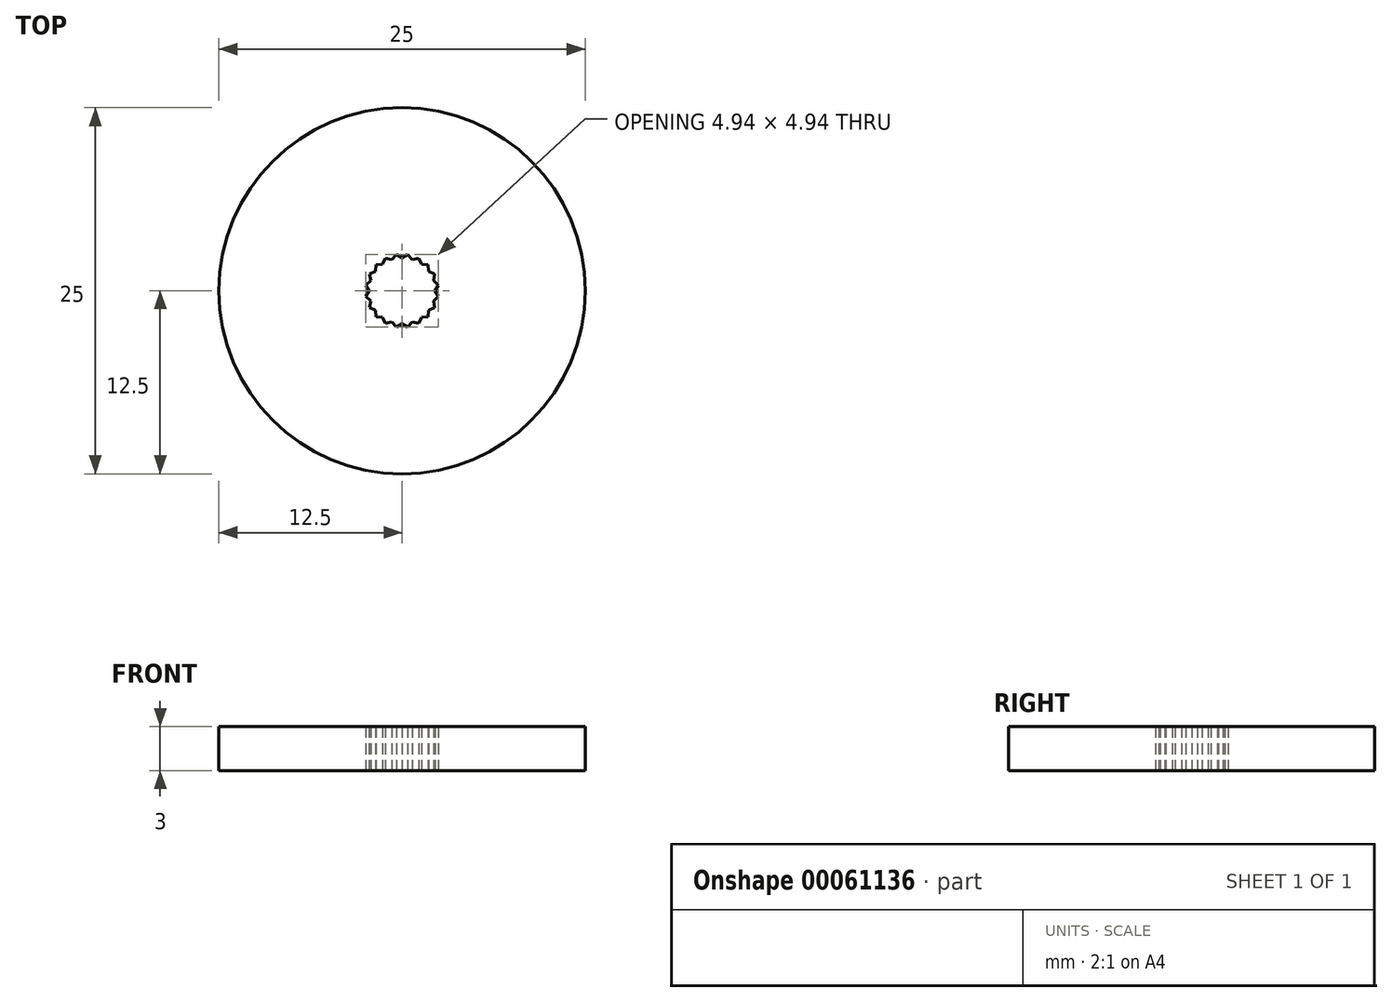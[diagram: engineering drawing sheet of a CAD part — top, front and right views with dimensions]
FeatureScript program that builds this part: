
annotation { "Feature Type Name" : "Feature", "Feature Type Description" : "" }
export const myFeature = defineFeature(function(context is Context, id is Id, definition is map)
    precondition{}
    {
        {
            var Q0;
            Q0=qCreatedBy(makeId("Top.planeOp"),FACE);
            var sketch = newSketch(context, id + "F0", { "sketchPlane" : qUnion([Q0])});
            skCircle(sketch, "E0", {"center": v(0, 0) * mm, "radius": 12.5 * mm});
            skCircle(sketch, "E1", {"center": v(0, 0) * mm, "radius": 2.25 * mm, "construction": true});
            skLineSegment(sketch, "E2", {"start": v(0, 0) * mm, "end": v(2.25, 0) * mm, "construction": true});
            skLineSegment(sketch, "E3", {"start": v(0, 0) * mm, "end": v(2.14, -0.7) * mm, "construction": true});
            skCircle(sketch, "E4", {"center": v(0, 0) * mm, "radius": 2.5 * mm, "construction": true});
            skLineSegment(sketch, "E5", {"start": v(0, 0) * mm, "end": v(2.47, -0.4) * mm, "construction": true});
            skLineSegment(sketch, "E6", {"start": v(2.25, 0) * mm, "end": v(2.47, -0.4) * mm});
            skLineSegment(sketch, "E7", {"start": v(2.47, -0.4) * mm, "end": v(2.14, -0.7) * mm});
            skLineSegment(sketch, "E8.1.0", {"start": v(2.14, 0.7) * mm, "end": v(2.47, 0.4) * mm});
            skLineSegment(sketch, "E8.1.1", {"start": v(2.47, 0.4) * mm, "end": v(2.25, 0) * mm});
            skLineSegment(sketch, "E8.2.0", {"start": v(1.82, 1.32) * mm, "end": v(2.23, 1.13) * mm});
            skLineSegment(sketch, "E8.2.1", {"start": v(2.23, 1.13) * mm, "end": v(2.14, 0.7) * mm});
            skLineSegment(sketch, "E8.3.0", {"start": v(1.32, 1.82) * mm, "end": v(1.77, 1.77) * mm});
            skLineSegment(sketch, "E8.3.1", {"start": v(1.77, 1.77) * mm, "end": v(1.82, 1.32) * mm});
            skLineSegment(sketch, "E8.4.0", {"start": v(0.7, 2.14) * mm, "end": v(1.13, 2.23) * mm});
            skLineSegment(sketch, "E8.4.1", {"start": v(1.13, 2.23) * mm, "end": v(1.32, 1.82) * mm});
            skLineSegment(sketch, "E8.5.0", {"start": v(0, 2.25) * mm, "end": v(0.4, 2.47) * mm});
            skLineSegment(sketch, "E8.5.1", {"start": v(0.4, 2.47) * mm, "end": v(0.7, 2.14) * mm});
            skLineSegment(sketch, "E8.6.0", {"start": v(-0.7, 2.14) * mm, "end": v(-0.4, 2.47) * mm});
            skLineSegment(sketch, "E8.6.1", {"start": v(-0.4, 2.47) * mm, "end": v(0, 2.25) * mm});
            skLineSegment(sketch, "E8.7.0", {"start": v(-1.32, 1.82) * mm, "end": v(-1.13, 2.23) * mm});
            skLineSegment(sketch, "E8.7.1", {"start": v(-1.13, 2.23) * mm, "end": v(-0.7, 2.14) * mm});
            skLineSegment(sketch, "E8.8.0", {"start": v(-1.82, 1.32) * mm, "end": v(-1.77, 1.77) * mm});
            skLineSegment(sketch, "E8.8.1", {"start": v(-1.77, 1.77) * mm, "end": v(-1.32, 1.82) * mm});
            skLineSegment(sketch, "E8.9.0", {"start": v(-2.14, 0.7) * mm, "end": v(-2.23, 1.13) * mm});
            skLineSegment(sketch, "E8.9.1", {"start": v(-2.23, 1.13) * mm, "end": v(-1.82, 1.32) * mm});
            skLineSegment(sketch, "E8.10.0", {"start": v(-2.25, 0) * mm, "end": v(-2.47, 0.4) * mm});
            skLineSegment(sketch, "E8.10.1", {"start": v(-2.47, 0.4) * mm, "end": v(-2.14, 0.7) * mm});
            skLineSegment(sketch, "E8.11.0", {"start": v(-2.14, -0.7) * mm, "end": v(-2.47, -0.4) * mm});
            skLineSegment(sketch, "E8.11.1", {"start": v(-2.47, -0.4) * mm, "end": v(-2.25, 0) * mm});
            skLineSegment(sketch, "E8.12.0", {"start": v(-1.82, -1.32) * mm, "end": v(-2.23, -1.13) * mm});
            skLineSegment(sketch, "E8.12.1", {"start": v(-2.23, -1.13) * mm, "end": v(-2.14, -0.7) * mm});
            skLineSegment(sketch, "E8.13.0", {"start": v(-1.32, -1.82) * mm, "end": v(-1.77, -1.77) * mm});
            skLineSegment(sketch, "E8.13.1", {"start": v(-1.77, -1.77) * mm, "end": v(-1.82, -1.32) * mm});
            skLineSegment(sketch, "E8.14.0", {"start": v(-0.7, -2.14) * mm, "end": v(-1.13, -2.23) * mm});
            skLineSegment(sketch, "E8.14.1", {"start": v(-1.13, -2.23) * mm, "end": v(-1.32, -1.82) * mm});
            skLineSegment(sketch, "E8.15.0", {"start": v(0, -2.25) * mm, "end": v(-0.4, -2.47) * mm});
            skLineSegment(sketch, "E8.15.1", {"start": v(-0.4, -2.47) * mm, "end": v(-0.7, -2.14) * mm});
            skLineSegment(sketch, "E8.16.0", {"start": v(0.7, -2.14) * mm, "end": v(0.4, -2.47) * mm});
            skLineSegment(sketch, "E8.16.1", {"start": v(0.4, -2.47) * mm, "end": v(0, -2.25) * mm});
            skLineSegment(sketch, "E8.17.0", {"start": v(1.32, -1.82) * mm, "end": v(1.13, -2.23) * mm});
            skLineSegment(sketch, "E8.17.1", {"start": v(1.13, -2.23) * mm, "end": v(0.7, -2.14) * mm});
            skLineSegment(sketch, "E8.18.0", {"start": v(1.82, -1.32) * mm, "end": v(1.77, -1.77) * mm});
            skLineSegment(sketch, "E8.18.1", {"start": v(1.77, -1.77) * mm, "end": v(1.32, -1.82) * mm});
            skLineSegment(sketch, "E8.19.0", {"start": v(2.14, -0.7) * mm, "end": v(2.23, -1.13) * mm});
            skLineSegment(sketch, "E8.19.1", {"start": v(2.23, -1.13) * mm, "end": v(1.82, -1.32) * mm});
            skSolve(sketch);
        }
        {
            var Q0;
            Q0=makeQuery(id+"F0.imprint","IMPRINT",FACE,{"disambiguationData":[TD([[makeQuery(id+"F0.imprint","IMPRINT",EDGE,{"derivedFrom":sQuery(id+"F0.wireOp",EDGE,"E0")}),1.0]])]});
            extrude(context, id + "F1", {"entities" : qUnion([Q0]), "depth" : 3 * mm});
        }
    });
